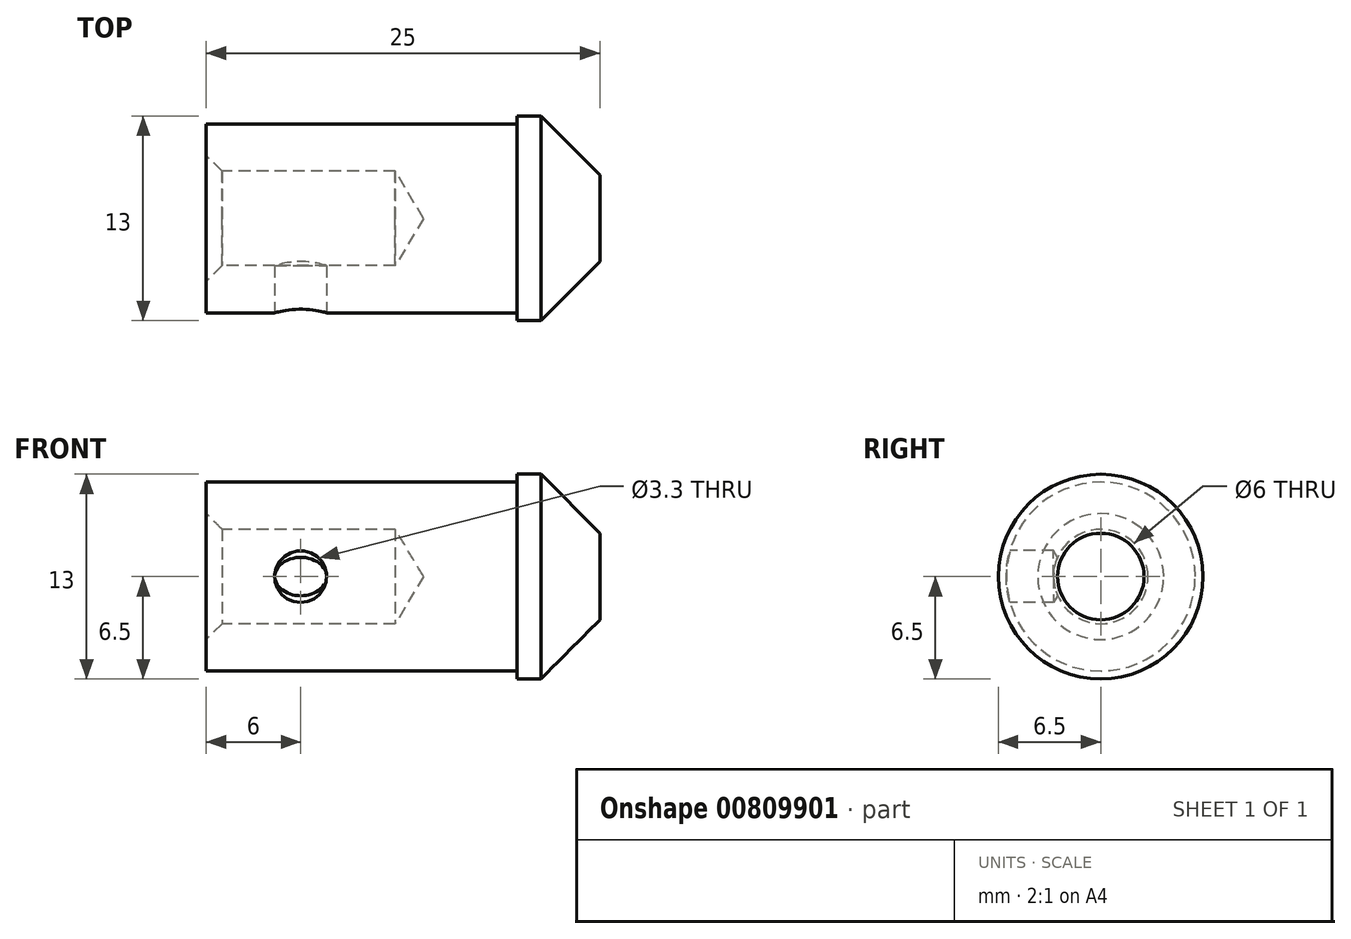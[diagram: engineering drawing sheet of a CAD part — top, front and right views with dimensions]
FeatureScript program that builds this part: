
annotation { "Feature Type Name" : "Feature", "Feature Type Description" : "" }
export const myFeature = defineFeature(function(context is Context, id is Id, definition is map)
    precondition{}
    {
        {
            var Q0;
            Q0=qCreatedBy(makeId("Front.planeOp"),FACE);
            var sketch = newSketch(context, id + "F0", { "sketchPlane" : qUnion([Q0])});
            skLineSegment(sketch, "E0", {"start": v(0, 0) * mm, "end": v(0, 6) * mm});
            skLineSegment(sketch, "E1", {"start": v(0, 6) * mm, "end": v(19.75, 6) * mm});
            skLineSegment(sketch, "E2", {"start": v(19.75, 6) * mm, "end": v(19.75, 6.5) * mm});
            skLineSegment(sketch, "E3", {"start": v(19.75, 6.5) * mm, "end": v(21.25, 6.5) * mm});
            skLineSegment(sketch, "E4", {"start": v(21.25, 6.5) * mm, "end": v(25, 2.75) * mm});
            skLineSegment(sketch, "E5", {"start": v(25, 2.75) * mm, "end": v(25, 0) * mm});
            skLineSegment(sketch, "E6", {"start": v(25, 0) * mm, "end": v(0, 0) * mm});
            skSolve(sketch);
        }
        {
            var Q0;
            Q0 = qSketchRegion(id + "F0", true);
            var Q1;
            Q1=sQuery(id+"F0.wireOp",EDGE,"E6");
            revolve(context, id + "F1", {"surfaceOperationType" : NewSurfaceOperationType.NEW, "entities" : qUnion([Q0]), "axis" : qUnion([Q1]), "revolveType" : RevolveType.FULL});
        }
        {
            var Q0;
            Q0=makeQuery(id+"F1.opRevolve","SWEPT_FACE",FACE,{"disambiguationData":[OSD([sQuery(id+"F0.wireOp",EDGE,"E0")])]});
            var sketch = newSketch(context, id + "F2", { "sketchPlane" : qUnion([Q0])});
            skPoint(sketch, "E7", {"position": v(0, 0) * mm});
            skSolve(sketch);
        }
        {
            var Q0;
            Q0=sQuery(id+"F2.wireOp",VERTEX,"E7");
            var Q1;
            Q1=makeQuery(id+"F1.opRevolve","SWEPT_BODY",BODY,{"disambiguationData":[OSD([sQuery(id+"F0.wireOp",EDGE,"E0"),sQuery(id+"F0.wireOp",EDGE,"E1"),sQuery(id+"F0.wireOp",EDGE,"E2"),sQuery(id+"F0.wireOp",EDGE,"E3"),sQuery(id+"F0.wireOp",EDGE,"E4"),sQuery(id+"F0.wireOp",EDGE,"E5"),sQuery(id+"F0.wireOp",EDGE,"E6")])]});
            hole(context, id + "F3", {"style" : HoleStyle.C_SINK, "endStyle" : HoleEndStyle.BLIND, "holeDiameter" : 6 * mm, "cSinkDiameter" : 8 * mm, "cSinkAngle" : 90 * degree, "majorDiameter" : 5 * mm, "holeDepth" : 12 * mm, "isTappedThrough" : true, "tappedDepth" : 12 * mm, "tapClearance" : 3, "startFromSketch" : true, "locations" : qUnion([Q0]), "scope" : qUnion([Q1])});
        }
        {
            var Q0;
            Q0=qCreatedBy(makeId("Front.planeOp"),FACE);
            cPlane(context, id + "F4", {"entities" : qUnion([Q0]), "cplaneType" : CPlaneType.OFFSET, "offset" : 7 * mm, "width" : 150 * mm, "height" : 150 * mm});
        }
        {
            var Q0;
            Q0=qCreatedBy(id+"F4.planeOp",FACE);
            var sketch = newSketch(context, id + "F5", { "sketchPlane" : qUnion([Q0])});
            skPoint(sketch, "E8", {"position": v(6, 0) * mm});
            skSolve(sketch);
        }
        {
            var Q0;
            Q0=sQuery(id+"F5.wireOp",VERTEX,"E8");
            var Q1;
            Q1=makeQuery(id+"F1.opRevolve","SWEPT_BODY",BODY,{"disambiguationData":[OSD([sQuery(id+"F0.wireOp",EDGE,"E0"),sQuery(id+"F0.wireOp",EDGE,"E1"),sQuery(id+"F0.wireOp",EDGE,"E2"),sQuery(id+"F0.wireOp",EDGE,"E3"),sQuery(id+"F0.wireOp",EDGE,"E4"),sQuery(id+"F0.wireOp",EDGE,"E5"),sQuery(id+"F0.wireOp",EDGE,"E6")])]});
            hole(context, id + "F6", {"style" : HoleStyle.SIMPLE, "endStyle" : HoleEndStyle.BLIND, "standardTappedOrClearance" : lookupTablePath({ "standard" : "ISO", "fit" : "Normal", "size" : "M3", "type" : "Clearance" }), "standardBlindInLast" : lookupTablePath({ "fit" : "Standard", "standard" : "ISO", "size" : "M3", "type" : "Clearance" }), "holeDiameter" : 3.3 * mm, "majorDiameter" : 5 * mm, "holeDepth" : 4 * mm, "isTappedThrough" : true, "tappedDepth" : 12 * mm, "tapClearance" : 3, "startFromSketch" : true, "locations" : qUnion([Q0]), "scope" : qUnion([Q1])});
        }
    });
